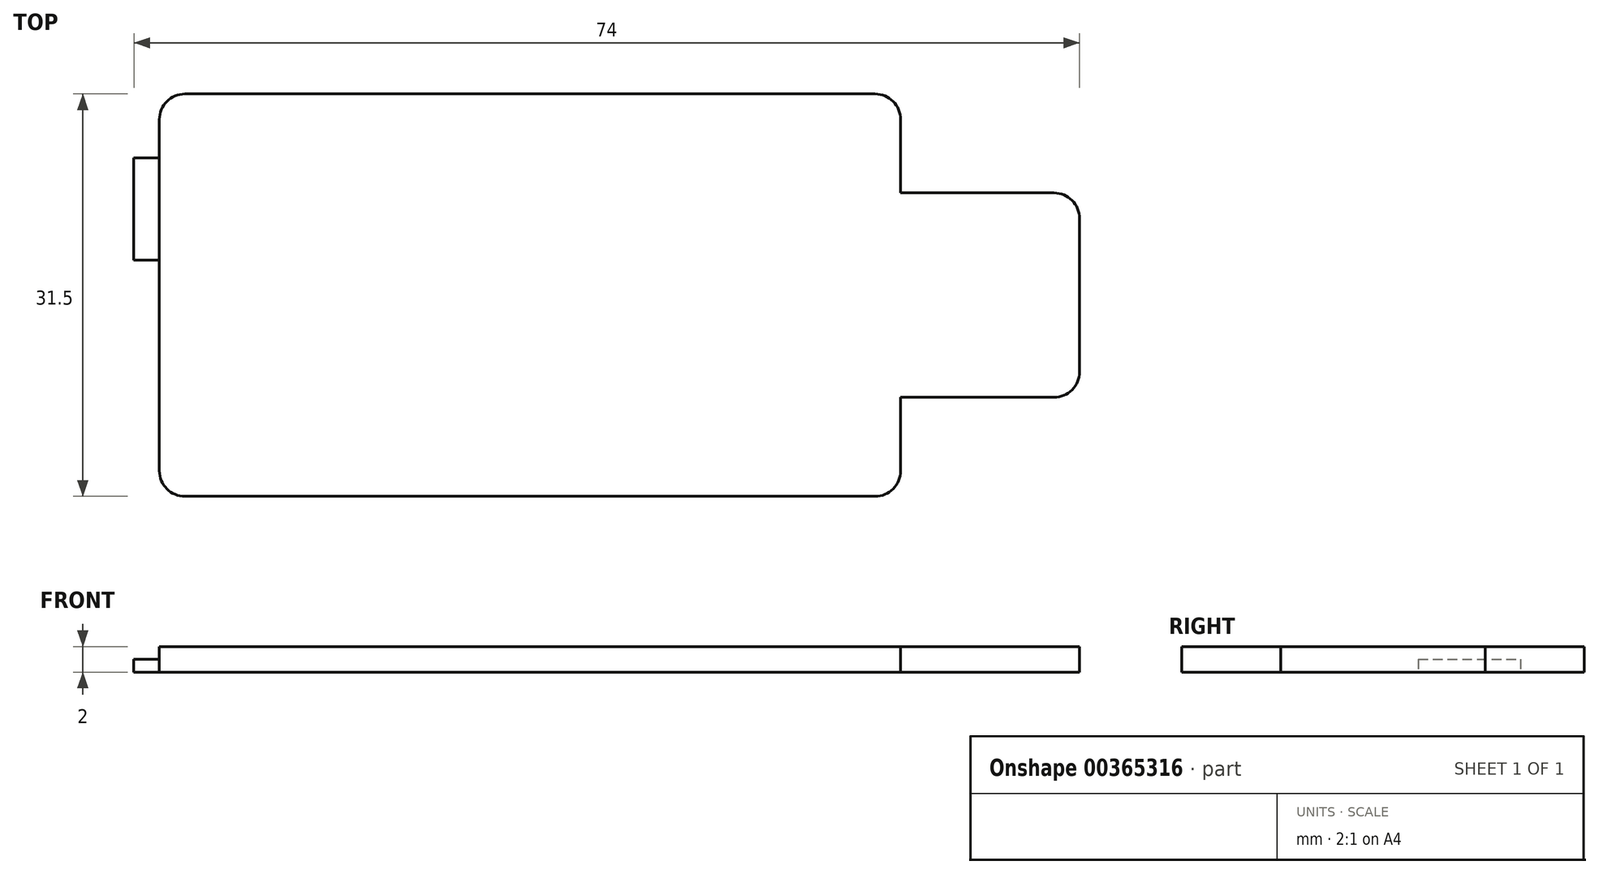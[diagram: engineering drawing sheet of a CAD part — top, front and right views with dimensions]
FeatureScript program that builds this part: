
annotation { "Feature Type Name" : "Feature", "Feature Type Description" : "" }
export const myFeature = defineFeature(function(context is Context, id is Id, definition is map)
    precondition{}
    {
        {
            var Q0;
            Q0=qCreatedBy(makeId("Top.planeOp"),FACE);
            var sketch = newSketch(context, id + "F0", { "sketchPlane" : qUnion([Q0])});
            skLineSegment(sketch, "E0.bottom", {"start": v(10.18, -15.75) * mm, "end": v(-47.82, -15.75) * mm});
            skLineSegment(sketch, "E0.top", {"start": v(10.18, 15.75) * mm, "end": v(-47.82, 15.75) * mm});
            skLineSegment(sketch, "E0.left", {"start": v(10.18, -15.75) * mm, "end": v(10.18, 15.75) * mm});
            skLineSegment(sketch, "E0.right", {"start": v(-47.82, -15.75) * mm, "end": v(-47.82, 15.75) * mm});
            skPoint(sketch, "E0.middle", {"position": v(-18.82, 0) * mm});
            skLineSegment(sketch, "E1.bottom", {"start": v(24.18, -8) * mm, "end": v(-3.82, -8) * mm});
            skLineSegment(sketch, "E1.top", {"start": v(24.18, 8) * mm, "end": v(-3.82, 8) * mm});
            skLineSegment(sketch, "E1.left", {"start": v(24.18, -8) * mm, "end": v(24.18, 8) * mm});
            skLineSegment(sketch, "E1.right", {"start": v(-3.82, -8) * mm, "end": v(-3.82, 8) * mm});
            skPoint(sketch, "E1.middle", {"position": v(10.18, 0) * mm});
            skLineSegment(sketch, "E2.bottom", {"start": v(-47.82, 2.75) * mm, "end": v(-49.82, 2.75) * mm});
            skLineSegment(sketch, "E2.top", {"start": v(-47.82, 10.75) * mm, "end": v(-49.82, 10.75) * mm});
            skLineSegment(sketch, "E2.left", {"start": v(-47.82, 2.75) * mm, "end": v(-47.82, 10.75) * mm});
            skLineSegment(sketch, "E2.right", {"start": v(-49.82, 2.75) * mm, "end": v(-49.82, 10.75) * mm});
            skPoint(sketch, "E2.middle", {"position": v(-48.82, 6.75) * mm});
            skLineSegment(sketch, "E3.MirrorCS", {"start": v(-47.82, -2.75) * mm, "end": v(-47.82, -10.75) * mm});
            skLineSegment(sketch, "E4.MirrorCS", {"start": v(-47.82, -10.75) * mm, "end": v(-49.82, -10.75) * mm});
            skLineSegment(sketch, "E5.MirrorCS", {"start": v(-49.82, -2.75) * mm, "end": v(-49.82, -10.75) * mm});
            skLineSegment(sketch, "E6.MirrorCS", {"start": v(-47.82, -2.75) * mm, "end": v(-49.82, -2.75) * mm});
            skSolve(sketch);
        }
        {
            var Q0;
            {var subQ8=sQuery(id+"F0.wireOp",EDGE,"E0.bottom");Q0=makeQuery(id+"F0.imprint","IMPRINT",FACE,{"disambiguationData":[TD([[makeQuery(id+"F0.imprint","IMPRINT",EDGE,{"derivedFrom":subQ8}),-1.0]])]});}
            var Q1;
            {var subQ5=sQuery(id+"F0.wireOp",EDGE,"E1.right");Q1=makeQuery(id+"F0.imprint","IMPRINT",FACE,{"disambiguationData":[TD([[makeQuery(id+"F0.imprint","IMPRINT",EDGE,{"derivedFrom":subQ5}),-1.0]])]});}
            var Q2;
            {var subQ5=sQuery(id+"F0.wireOp",EDGE,"E1.left");Q2=makeQuery(id+"F0.imprint","IMPRINT",FACE,{"disambiguationData":[TD([[makeQuery(id+"F0.imprint","IMPRINT",EDGE,{"derivedFrom":subQ5}),1.0]])]});}
            extrude(context, id + "F1", {"entities" : qUnion([Q0, Q1, Q2]), "depth" : 2 * mm});
        }
        {
            var Q0;
            Q0=makeQuery(id+"F0.imprint","IMPRINT",FACE,{"disambiguationData":[TD([[makeQuery(id+"F0.imprint","IMPRINT",EDGE,{"derivedFrom":sQuery(id+"F0.wireOp",EDGE,"E2.bottom")}),-1.0]])]});
            var Q1;
            Q1=makeQuery(id+"F0.imprint","IMPRINT",FACE,{"disambiguationData":[TD([[makeQuery(id+"F0.imprint","IMPRINT",EDGE,{"derivedFrom":sQuery(id+"F0.wireOp",EDGE,"E3.MirrorCS")}),-1.0]])]});
            extrude(context, id + "F2", {"entities" : qUnion([Q0, Q1]), "operationType" : NewBodyOperationType.ADD, "depth" : 1 * mm});
        }
        {
            var Q0;
            Q0=makeQuery(id+"F1.opExtrude","SWEPT_EDGE",EDGE,{"disambiguationData":[OSD([sQuery(id+"F0.wireOp",EDGE,"E0.top"),sQuery(id+"F0.wireOp",EDGE,"E0.left")])]});
            var Q1;
            Q1=makeQuery(id+"F1.opExtrude","SWEPT_EDGE",EDGE,{"disambiguationData":[OSD([sQuery(id+"F0.wireOp",EDGE,"E1.top"),sQuery(id+"F0.wireOp",EDGE,"E1.left")])]});
            var Q2;
            Q2=makeQuery(id+"F1.opExtrude","SWEPT_EDGE",EDGE,{"disambiguationData":[OSD([sQuery(id+"F0.wireOp",EDGE,"E1.bottom"),sQuery(id+"F0.wireOp",EDGE,"E1.left")])]});
            var Q3;
            Q3=makeQuery(id+"F1.opExtrude","SWEPT_EDGE",EDGE,{"disambiguationData":[OSD([sQuery(id+"F0.wireOp",EDGE,"E0.bottom"),sQuery(id+"F0.wireOp",EDGE,"E0.left")])]});
            var Q4;
            Q4=makeQuery(id+"F1.opExtrude","SWEPT_EDGE",EDGE,{"disambiguationData":[OSD([sQuery(id+"F0.wireOp",EDGE,"E0.bottom"),sQuery(id+"F0.wireOp",EDGE,"E0.right")])]});
            var Q5;
            Q5=makeQuery(id+"F1.opExtrude","SWEPT_EDGE",EDGE,{"disambiguationData":[OSD([sQuery(id+"F0.wireOp",EDGE,"E0.top"),sQuery(id+"F0.wireOp",EDGE,"E0.right")])]});
            fillet(context, id + "F3", {"entities" : qUnion([Q0, Q1, Q2, Q3, Q4, Q5]), "radius" : 2 * mm, "tangentPropagation" : true, "allowEdgeOverflow" : false});
        }
    });
